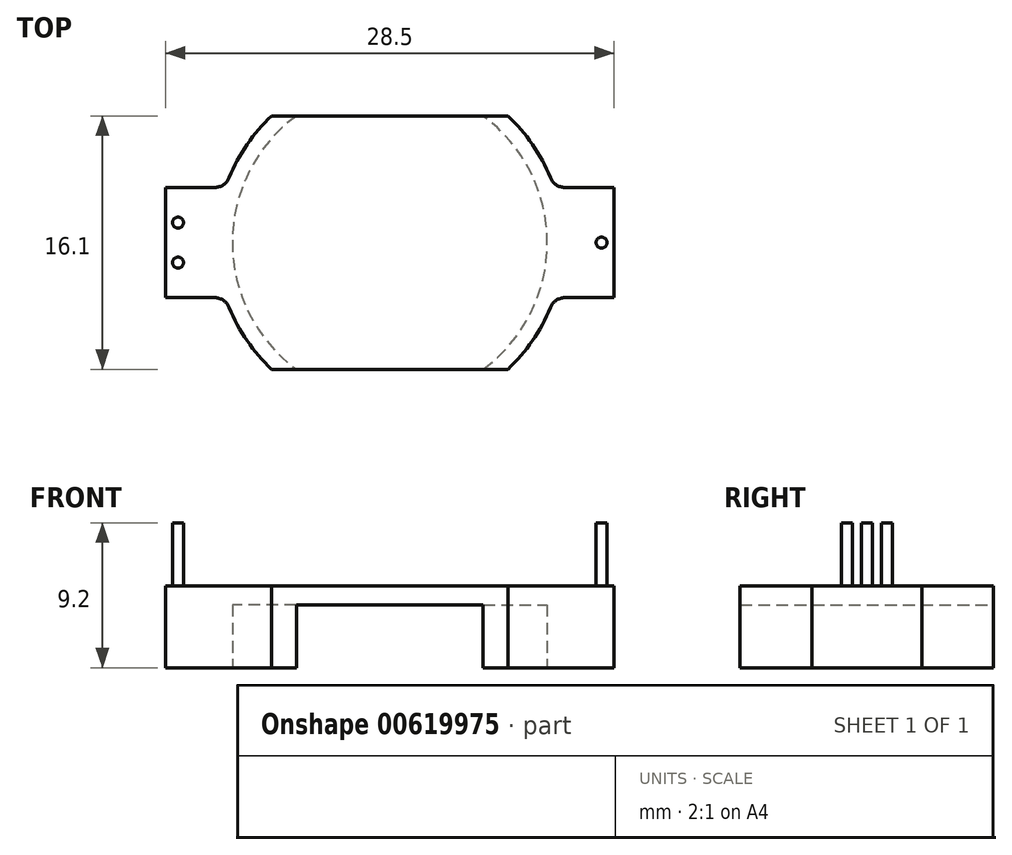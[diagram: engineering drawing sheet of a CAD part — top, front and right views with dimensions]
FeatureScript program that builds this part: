
annotation { "Feature Type Name" : "Feature", "Feature Type Description" : "" }
export const myFeature = defineFeature(function(context is Context, id is Id, definition is map)
    precondition{}
    {
        {
            var Q0;
            Q0=qCreatedBy(makeId("Top.planeOp"),FACE);
            var sketch = newSketch(context, id + "F0", { "sketchPlane" : qUnion([Q0])});
            skArc(sketch, "E0", {"start": v(-7.5, 8.05) * mm, "mid": v(-9.06, 6.24) * mm, "end": v(-10.2, 4.13) * mm});
            skLineSegment(sketch, "E1", {"start": v(-7.5, -8.05) * mm, "end": v(7.5, -8.05) * mm});
            skLineSegment(sketch, "E2", {"start": v(-7.5, 8.05) * mm, "end": v(7.5, 8.05) * mm});
            skArc(sketch, "E3.trimOffspring", {"start": v(7.5, -8.05) * mm, "mid": v(9.06, -6.24) * mm, "end": v(10.2, -4.13) * mm});
            skLineSegment(sketch, "E4.bottom", {"start": v(14.25, 3.5) * mm, "end": v(11.12, 3.5) * mm});
            skLineSegment(sketch, "E4.top", {"start": v(14.25, -3.5) * mm, "end": v(11.12, -3.5) * mm});
            skLineSegment(sketch, "E4.left", {"start": v(14.25, 3.5) * mm, "end": v(14.25, -3.5) * mm});
            skLineSegment(sketch, "E4.right", {"start": v(-14.25, 3.5) * mm, "end": v(-14.25, -3.5) * mm});
            skLineSegment(sketch, "E5.trimOffspring", {"start": v(-11.12, 3.5) * mm, "end": v(-14.25, 3.5) * mm});
            skLineSegment(sketch, "E6.trimOffspring", {"start": v(-11.12, -3.5) * mm, "end": v(-14.25, -3.5) * mm});
            skArc(sketch, "E7.trimOffspring", {"start": v(-10.2, -4.12) * mm, "mid": v(-9.06, -6.24) * mm, "end": v(-7.5, -8.05) * mm});
            skArc(sketch, "E8.trimOffspring", {"start": v(10.2, 4.13) * mm, "mid": v(9.06, 6.24) * mm, "end": v(7.5, 8.05) * mm});
            skPoint(sketch, "E9.visualSharp", {"position": v(-10.43, 3.5) * mm});
            skArc(sketch, "E9.filletArc", {"start": v(-11.12, 3.5) * mm, "mid": v(-10.57, 3.67) * mm, "end": v(-10.2, 4.13) * mm});
            skPoint(sketch, "E10.visualSharp", {"position": v(-10.43, -3.5) * mm});
            skArc(sketch, "E10.filletArc", {"start": v(-10.2, -4.13) * mm, "mid": v(-10.57, -3.67) * mm, "end": v(-11.12, -3.5) * mm});
            skPoint(sketch, "E11.visualSharp", {"position": v(10.43, -3.5) * mm});
            skArc(sketch, "E11.filletArc", {"start": v(11.12, -3.5) * mm, "mid": v(10.57, -3.67) * mm, "end": v(10.2, -4.13) * mm});
            skPoint(sketch, "E12.visualSharp", {"position": v(10.43, 3.5) * mm});
            skArc(sketch, "E12.filletArc", {"start": v(10.2, 4.13) * mm, "mid": v(10.57, 3.67) * mm, "end": v(11.12, 3.5) * mm});
            skSolve(sketch);
        }
        {
            var Q0;
            Q0 = qSketchRegion(id + "F0", true);
            extrude(context, id + "F1", {"entities" : qUnion([Q0]), "depth" : 5.2 * mm, "offsetDistance" : 25 * mm});
        }
        {
            var Q0;
            Q0=makeQuery(id+"F1.opExtrude","CAP_FACE",FACE,{"disambiguationData":[OSD([sQuery(id+"F0.wireOp",EDGE,"E0"),sQuery(id+"F0.wireOp",EDGE,"E1"),sQuery(id+"F0.wireOp",EDGE,"E2"),sQuery(id+"F0.wireOp",EDGE,"E3.trimOffspring"),sQuery(id+"F0.wireOp",EDGE,"E4.bottom"),sQuery(id+"F0.wireOp",EDGE,"E4.top"),sQuery(id+"F0.wireOp",EDGE,"E4.left"),sQuery(id+"F0.wireOp",EDGE,"E4.right"),sQuery(id+"F0.wireOp",EDGE,"E5.trimOffspring"),sQuery(id+"F0.wireOp",EDGE,"E6.trimOffspring"),sQuery(id+"F0.wireOp",EDGE,"E7.trimOffspring"),sQuery(id+"F0.wireOp",EDGE,"E8.trimOffspring"),sQuery(id+"F0.wireOp",EDGE,"E9.filletArc"),sQuery(id+"F0.wireOp",EDGE,"E10.filletArc"),sQuery(id+"F0.wireOp",EDGE,"E11.filletArc"),sQuery(id+"F0.wireOp",EDGE,"E12.filletArc")])],"isStart":true});
            var sketch = newSketch(context, id + "F2", { "sketchPlane" : qUnion([Q0])});
            skCircle(sketch, "E13", {"center": v(0, 0) * mm, "radius": 10 * mm});
            skSolve(sketch);
        }
        {
            var Q0;
            Q0 = qSketchRegion(id + "F2", true);
            extrude(context, id + "F3", {"entities" : qUnion([Q0]), "operationType" : NewBodyOperationType.REMOVE, "oppositeDirection" : true, "depth" : 4 * mm, "offsetDistance" : 25 * mm});
        }
        {
            var Q0;
            Q0=makeQuery(id+"F1.opExtrude","CAP_FACE",FACE,{"disambiguationData":[OSD([sQuery(id+"F0.wireOp",EDGE,"E0"),sQuery(id+"F0.wireOp",EDGE,"E1"),sQuery(id+"F0.wireOp",EDGE,"E2"),sQuery(id+"F0.wireOp",EDGE,"E3.trimOffspring"),sQuery(id+"F0.wireOp",EDGE,"E4.bottom"),sQuery(id+"F0.wireOp",EDGE,"E4.top"),sQuery(id+"F0.wireOp",EDGE,"E4.left"),sQuery(id+"F0.wireOp",EDGE,"E4.right"),sQuery(id+"F0.wireOp",EDGE,"E5.trimOffspring"),sQuery(id+"F0.wireOp",EDGE,"E6.trimOffspring"),sQuery(id+"F0.wireOp",EDGE,"E7.trimOffspring"),sQuery(id+"F0.wireOp",EDGE,"E8.trimOffspring"),sQuery(id+"F0.wireOp",EDGE,"E9.filletArc"),sQuery(id+"F0.wireOp",EDGE,"E10.filletArc"),sQuery(id+"F0.wireOp",EDGE,"E11.filletArc"),sQuery(id+"F0.wireOp",EDGE,"E12.filletArc")])],"isStart":false});
            var sketch = newSketch(context, id + "F4", { "sketchPlane" : qUnion([Q0])});
            skCircle(sketch, "E14", {"center": v(13.45, 0) * mm, "radius": 0.35 * mm});
            skCircle(sketch, "E15", {"center": v(-13.45, 1.27) * mm, "radius": 0.35 * mm});
            skCircle(sketch, "E16", {"center": v(-13.45, -1.27) * mm, "radius": 0.35 * mm});
            skSolve(sketch);
        }
        {
            var Q0;
            Q0 = qSketchRegion(id + "F4", true);
            extrude(context, id + "F5", {"entities" : qUnion([Q0]), "operationType" : NewBodyOperationType.ADD, "depth" : 4 * mm, "offsetDistance" : 25 * mm});
        }
    });
